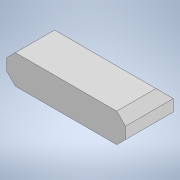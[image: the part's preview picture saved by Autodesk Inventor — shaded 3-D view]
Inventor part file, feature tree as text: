
AUTODESK INVENTOR PART (.ipt)
format: ipt  version: 2021 (Build 250183000, 183)  size: 122,368 bytes
history: native  units: mm
features: extrude x2, chamfer x2, sketch x2
ambient origin geometry x8: Origin, YZ Plane, XZ Plane, XY Plane, X Axis, Y Axis, Z Axis, Center Point
bodies: Solid1 (feature_tree)
feature tree (6):
  extrude  "Extrusion1"  Depth=3.0mm
  chamfer  "Chamfer1"  Distance=34.0mm
  extrude  "Extrusion4"  Depth=3.0mm
  chamfer  "Chamfer2"  Distance=16.0mm
  sketch  "Sketch1"  dims[d0=3.0mm d1=3.0mm]
  sketch  "Sketch4"  dims[d2=10.0mm d3=34.0mm d4=0.15mm d5=16.0mm d6=0.0mm d21=2.9mm d22=2.0mm d23=45.0deg d24=7.0mm d25=4.0mm d26=16.0mm d27=3.0mm d28=0.0mm d29=3.0mm d30=2.0mm d31=45.0deg]
